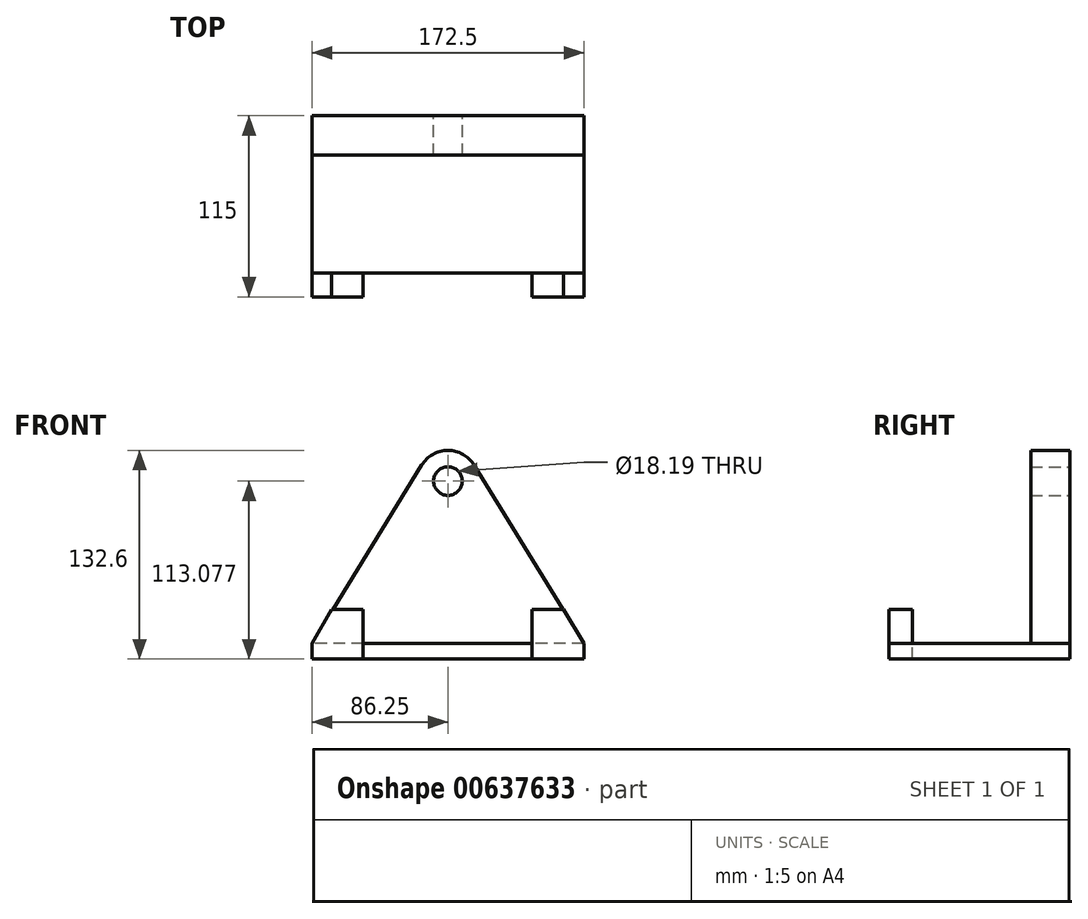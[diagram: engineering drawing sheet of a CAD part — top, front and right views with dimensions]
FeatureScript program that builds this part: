
annotation { "Feature Type Name" : "Feature", "Feature Type Description" : "" }
export const myFeature = defineFeature(function(context is Context, id is Id, definition is map)
    precondition{}
    {
        {
            var Q0;
            Q0=qCreatedBy(makeId("Front.planeOp"),FACE);
            var sketch = newSketch(context, id + "F0", { "sketchPlane" : qUnion([Q0])});
            skLineSegment(sketch, "E0", {"start": v(0, 0) * mm, "end": v(-172.5, 0) * mm});
            skArc(sketch, "E1", {"start": v(-69.62, 113.3) * mm, "mid": v(-86.25, 122.6) * mm, "end": v(-102.88, 113.3) * mm});
            skPoint(sketch, "E1.centerSnap0", {"position": v(-86.25, 0) * mm});
            skCircle(sketch, "E2", {"center": v(-86.25, 103.08) * mm, "radius": 9.1 * mm});
            skLineSegment(sketch, "E3", {"start": v(-172.5, 0) * mm, "end": v(-102.88, 113.3) * mm});
            skLineSegment(sketch, "E4", {"start": v(0, 0) * mm, "end": v(-69.62, 113.3) * mm});
            skLineSegment(sketch, "E5", {"start": v(-172.5, 0) * mm, "end": v(-172.5, -10) * mm});
            skLineSegment(sketch, "E6", {"start": v(-172.5, -10) * mm, "end": v(0, -10) * mm});
            skLineSegment(sketch, "E7", {"start": v(0, -10) * mm, "end": v(0, 0) * mm});
            skLineSegment(sketch, "E8", {"start": v(-159.78, 20.7) * mm, "end": v(-139, 20.7) * mm});
            skLineSegment(sketch, "E9", {"start": v(-139, 20.7) * mm, "end": v(-139, -10) * mm});
            skLineSegment(sketch, "E10", {"start": v(-12.72, 20.7) * mm, "end": v(-33.8, 20.7) * mm});
            skLineSegment(sketch, "E11", {"start": v(-33.8, 20.7) * mm, "end": v(-33.8, -10) * mm});
            skSolve(sketch);
        }
        {
            var Q0;
            {var subQ4=sQuery(id+"F0.wireOp",EDGE,"E1");Q0=makeQuery(id+"F0.imprint","IMPRINT",FACE,{"disambiguationData":[TD([[makeQuery(id+"F0.imprint","IMPRINT",EDGE,{"derivedFrom":subQ4}),1.0]])]});}
            var Q1;
            {var subQ5=sQuery(id+"F0.wireOp",EDGE,"E8");Q1=makeQuery(id+"F0.imprint","IMPRINT",FACE,{"disambiguationData":[TD([[makeQuery(id+"F0.imprint","IMPRINT",EDGE,{"derivedFrom":subQ5}),-1.0]])]});}
            var Q2;
            {var subQ5=sQuery(id+"F0.wireOp",EDGE,"E10");Q2=makeQuery(id+"F0.imprint","IMPRINT",FACE,{"disambiguationData":[TD([[makeQuery(id+"F0.imprint","IMPRINT",EDGE,{"derivedFrom":subQ5}),1.0]])]});}
            extrude(context, id + "F1", {"entities" : qUnion([Q0, Q1, Q2]), "depth" : 25 * mm, "offsetDistance" : 25 * mm});
        }
        {
            var Q0;
            {var subQ0=sQuery(id+"F0.wireOp",EDGE,"E11");var subQ1=sQuery(id+"F0.wireOp",EDGE,"E0");var subQ2=makeQuery(id+"F0.imprint","INTERSECT",VERTEX,{"derivedFrom":[subQ1,subQ0]});Q0=makeQuery(id+"F0.imprint","IMPRINT",FACE,{"disambiguationData":[TD([[makeQuery(id+"F0.imprint","IMPRINT",EDGE,{"disambiguationData":[TD([[subQ2,-1.0]])],"derivedFrom":subQ1}),1.0]])]});}
            var Q1;
            {var subQ0=sQuery(id+"F0.wireOp",EDGE,"E5");Q1=makeQuery(id+"F0.imprint","IMPRINT",FACE,{"disambiguationData":[TD([[makeQuery(id+"F0.imprint","IMPRINT",EDGE,{"derivedFrom":subQ0}),1.0]])]});}
            var Q2;
            {var subQ0=sQuery(id+"F0.wireOp",EDGE,"E7");Q2=makeQuery(id+"F0.imprint","IMPRINT",FACE,{"disambiguationData":[TD([[makeQuery(id+"F0.imprint","IMPRINT",EDGE,{"derivedFrom":subQ0}),1.0]])]});}
            extrude(context, id + "F2", {"entities" : qUnion([Q0, Q1, Q2]), "operationType" : NewBodyOperationType.ADD, "depth" : 100 * mm, "offsetDistance" : 25 * mm});
        }
        {
            var Q0;
            Q0=makeQuery(id+"F2.opExtrude","CAP_FACE",FACE,{"disambiguationData":[OSD([sQuery(id+"F0.wireOp",EDGE,"E0"),sQuery(id+"F0.wireOp",EDGE,"E5"),sQuery(id+"F0.wireOp",EDGE,"E6"),sQuery(id+"F0.wireOp",EDGE,"E7")])],"isStart":false});
            var sketch = newSketch(context, id + "F3", { "sketchPlane" : qUnion([Q0])});
            skLineSegment(sketch, "E12", {"start": v(-160.05, 21.64) * mm, "end": v(-140.05, 21.64) * mm});
            skLineSegment(sketch, "E13", {"start": v(-140.05, 21.64) * mm, "end": v(-140.05, -10) * mm});
            skLineSegment(sketch, "E14", {"start": v(-140.05, -10) * mm, "end": v(-172.5, -10) * mm});
            skLineSegment(sketch, "E15", {"start": v(-172.5, -10) * mm, "end": v(-172.5, 0) * mm});
            skLineSegment(sketch, "E16", {"start": v(-172.5, 0) * mm, "end": v(-160.05, 21.64) * mm});
            skLineSegment(sketch, "E17", {"start": v(0, 0) * mm, "end": v(0, -10) * mm});
            skLineSegment(sketch, "E18", {"start": v(0, -10) * mm, "end": v(-32.87, -10) * mm});
            skLineSegment(sketch, "E19", {"start": v(-32.87, -10) * mm, "end": v(-32.87, 21.64) * mm});
            skLineSegment(sketch, "E20", {"start": v(-32.87, 21.64) * mm, "end": v(-12.87, 21.64) * mm});
            skLineSegment(sketch, "E21", {"start": v(-12.87, 21.64) * mm, "end": v(0, 0) * mm});
            skSolve(sketch);
        }
        {
            var Q0;
            Q0 = qSketchRegion(id + "F3", true);
            extrude(context, id + "F4", {"entities" : qUnion([Q0]), "operationType" : NewBodyOperationType.ADD, "depth" : 15 * mm, "offsetDistance" : 25 * mm});
        }
    });
